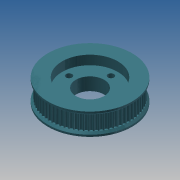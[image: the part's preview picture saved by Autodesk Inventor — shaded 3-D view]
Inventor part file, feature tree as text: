
AUTODESK INVENTOR PART (.ipt)
format: ipt  version: 2013 (Build 170138000, 138)  size: 357,376 bytes
history: native  units: mm
features: extrude x7, sketch x7, pattern_circular x2, chamfer x1, mirror x1
ambient origin geometry x8: Origin, YZ Plane, XZ Plane, XY Plane, X Axis, Y Axis, Z Axis, Center Point
bodies: Solid1 (feature_tree)
feature tree (18):
  extrude  "Extrusion1"  Depth=8.0mm TaperAngle=0.0deg
  extrude  "Extrusion3"  TaperAngle=0.0deg  [1 undecoded]
  extrude  "Extrusion4"  Depth=8.0mm TaperAngle=0.0deg
  pattern_circular  "Circular Pattern1"  Count=70 Angle=360.0deg
  extrude  "Extrusion5"  Depth=2.0mm TaperAngle=0.0deg
  chamfer  "Chamfer1"  Distance=1.0mm Angle=45.0deg
  mirror  "Mirror1"
  extrude  "Extrusion6"  Depth=2.0mm TaperAngle=0.0deg
  extrude  "Extrusion8"  Depth=5.0mm TaperAngle=0.0deg
  extrude  "Extrusion9"  Depth=11.5mm
  pattern_circular  "Circular Pattern2"  [2 undecoded]
  sketch  "Sketch1"  dims[d0=44.563384mm d9=8.0mm d10=0.0mm]
  sketch  "Sketch3"  dims[d22=0.254mm d23=0.0mm d24=0.0mm]
  sketch  "Sketch4"  dims[d25=1.59mm d27=8.0mm d28=0.0mm d29=700.0mm d30=360.0deg]
  sketch  "Sketch5"  dims[d33=1.0mm d34=2.0mm d35=0.0mm d36=1.0mm d37=2.0mm d38=45.0deg]
  sketch  "Sketch6"  dims[d39=15.5mm d41=2.0mm d42=0.0mm]
  sketch  "Sketch8"  dims[d46=30.5mm d48=5.0mm d49=0.0mm]
  sketch  "Sketch9"  dims[d50=3.3mm d52=11.5mm d53=5.0mm d54=0.0mm d55=40.0mm d56=360.0deg]
note: 3 required parameter values undecoded (feature->parameter linkage not recoverable at this tier; creation-order binding heuristic only, values carry confidence <= 0.55)
